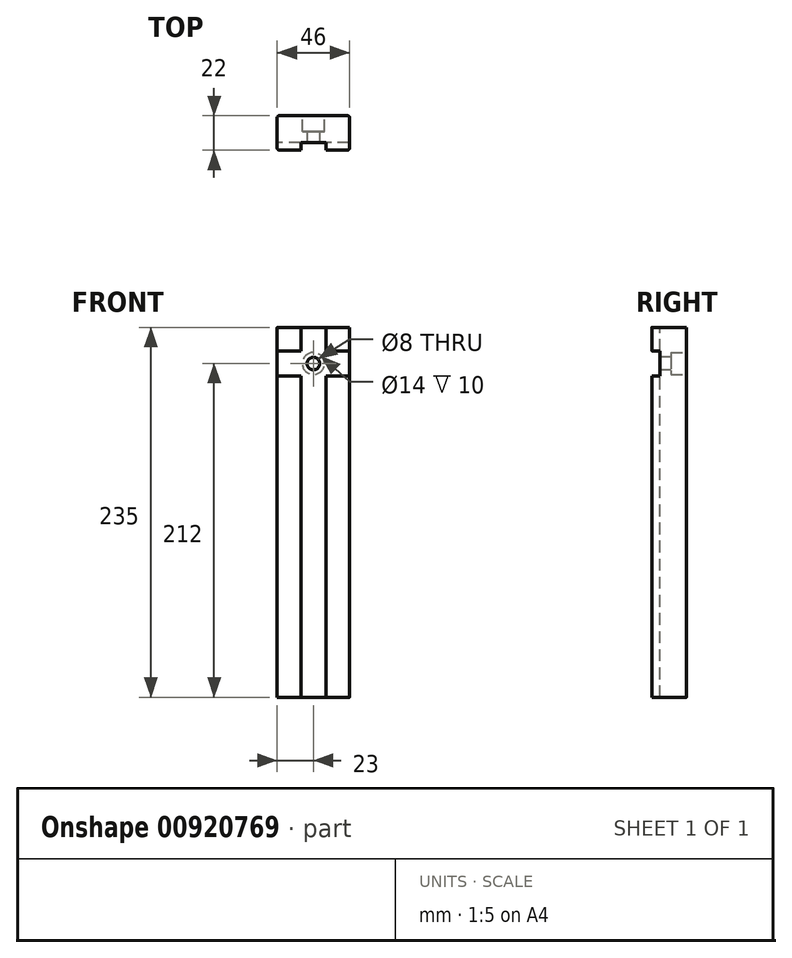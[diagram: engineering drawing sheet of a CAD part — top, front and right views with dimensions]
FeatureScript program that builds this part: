
annotation { "Feature Type Name" : "Feature", "Feature Type Description" : "" }
export const myFeature = defineFeature(function(context is Context, id is Id, definition is map)
    precondition{}
    {
        {
            var Q0;
            Q0=qCreatedBy(makeId("Top.planeOp"),FACE);
            var sketch = newSketch(context, id + "F0", { "sketchPlane" : qUnion([Q0])});
            skLineSegment(sketch, "E0.bottom", {"start": v(0, 0) * mm, "end": v(46, 0) * mm});
            skLineSegment(sketch, "E0.top", {"start": v(0, 22) * mm, "end": v(46, 22) * mm});
            skLineSegment(sketch, "E0.left", {"start": v(0, 0) * mm, "end": v(0, 22) * mm});
            skLineSegment(sketch, "E0.right", {"start": v(46, 0) * mm, "end": v(46, 22) * mm});
            skSolve(sketch);
        }
        {
            var Q0;
            Q0 = qSketchRegion(id + "F0", true);
            extrude(context, id + "F1", {"entities" : qUnion([Q0]), "depth" : 235 * mm, "offsetDistance" : 25 * mm});
        }
        {
            var Q0;
            Q0=makeQuery(id+"F1.opExtrude","SWEPT_EDGE",EDGE,{"disambiguationData":[OSD([sQuery(id+"F0.wireOp",EDGE,"E0.bottom"),sQuery(id+"F0.wireOp",EDGE,"E0.right")])]});
            var Q1;
            Q1=makeQuery(id+"F1.opExtrude","SWEPT_EDGE",EDGE,{"disambiguationData":[OSD([sQuery(id+"F0.wireOp",EDGE,"E0.top"),sQuery(id+"F0.wireOp",EDGE,"E0.right")])]});
            var Q2;
            Q2=makeQuery(id+"F1.opExtrude","SWEPT_EDGE",EDGE,{"disambiguationData":[OSD([sQuery(id+"F0.wireOp",EDGE,"E0.bottom"),sQuery(id+"F0.wireOp",EDGE,"E0.left")])]});
            var Q3;
            Q3=makeQuery(id+"F1.opExtrude","SWEPT_EDGE",EDGE,{"disambiguationData":[OSD([sQuery(id+"F0.wireOp",EDGE,"E0.top"),sQuery(id+"F0.wireOp",EDGE,"E0.left")])]});
            fillet(context, id + "F2", {"entities" : qUnion([Q0, Q1, Q2, Q3]), "radius" : 1.5 * mm, "tangentPropagation" : true, "allowEdgeOverflow" : false});
        }
        {
            var Q0;
            Q0=makeQuery(id+"F1.opExtrude","SWEPT_FACE",FACE,{"disambiguationData":[OSD([sQuery(id+"F0.wireOp",EDGE,"E0.left")])]});
            var sketch = newSketch(context, id + "F3", { "sketchPlane" : qUnion([Q0])});
            skLineSegment(sketch, "E1.bottom", {"start": v(-5, 220) * mm, "end": v(0, 220) * mm});
            skLineSegment(sketch, "E1.top", {"start": v(-5, 204) * mm, "end": v(0, 204) * mm});
            skLineSegment(sketch, "E1.left", {"start": v(-5, 220) * mm, "end": v(-5, 204) * mm});
            skLineSegment(sketch, "E1.right", {"start": v(0, 220) * mm, "end": v(0, 204) * mm});
            skSolve(sketch);
        }
        {
            var Q0;
            {var subQ0=sQuery(id+"F3.wireOp",EDGE,"E1.left");Q0=makeQuery(id+"F3.imprint","IMPRINT",FACE,{"disambiguationData":[TD([[makeQuery(id+"F3.imprint","IMPRINT",EDGE,{"derivedFrom":subQ0}),1.0]])]});}
            var Q1;
            {var subQ0=sQuery(id+"F3.wireOp",EDGE,"E1.right");Q1=makeQuery(id+"F3.imprint","IMPRINT",FACE,{"disambiguationData":[TD([[makeQuery(id+"F3.imprint","IMPRINT",EDGE,{"derivedFrom":subQ0}),-1.0]])]});}
            extrude(context, id + "F4", {"entities" : qUnion([Q0, Q1]), "operationType" : NewBodyOperationType.REMOVE, "endBound" : BoundingType.THROUGH_ALL, "oppositeDirection" : true, "depth" : 25 * mm, "offsetDistance" : 25 * mm});
        }
        {
            var Q0;
            Q0=makeQuery(id+"F1.opExtrude","CAP_FACE",FACE,{"disambiguationData":[OSD([sQuery(id+"F0.wireOp",EDGE,"E0.bottom"),sQuery(id+"F0.wireOp",EDGE,"E0.top"),sQuery(id+"F0.wireOp",EDGE,"E0.left"),sQuery(id+"F0.wireOp",EDGE,"E0.right")])],"isStart":false});
            var sketch = newSketch(context, id + "F5", { "sketchPlane" : qUnion([Q0])});
            skLineSegment(sketch, "E2.bottom", {"start": v(31, 0) * mm, "end": v(15, 0) * mm});
            skLineSegment(sketch, "E2.top", {"start": v(31, 5) * mm, "end": v(15, 5) * mm});
            skLineSegment(sketch, "E2.left", {"start": v(31, 0) * mm, "end": v(31, 5) * mm});
            skLineSegment(sketch, "E2.right", {"start": v(15, 0) * mm, "end": v(15, 5) * mm});
            skLineSegment(sketch, "E3", {"start": v(15, 2.5) * mm, "end": v(0, 2.5) * mm, "construction": true});
            skLineSegment(sketch, "E4", {"start": v(31, 2.5) * mm, "end": v(46, 2.5) * mm, "construction": true});
            skSolve(sketch);
        }
        {
            var Q0;
            Q0=makeQuery(id+"F5.imprint","IMPRINT",FACE,{"disambiguationData":[TD([[makeQuery(id+"F5.imprint","IMPRINT",EDGE,{"derivedFrom":sQuery(id+"F5.wireOp",EDGE,"E2.bottom")}),1.0]])]});
            extrude(context, id + "F6", {"entities" : qUnion([Q0]), "operationType" : NewBodyOperationType.REMOVE, "endBound" : BoundingType.THROUGH_ALL, "oppositeDirection" : true, "depth" : 25 * mm, "offsetDistance" : 25 * mm});
        }
        {
            var Q0;
            Q0=makeQuery(id+"F6.boolean.opBoolean","MERGE",FACE,{"derivedFrom":[makeQuery(id+"F4.boolean.opBoolean","COPY",FACE,{"derivedFrom":makeQuery(id+"F4.opExtrude","SWEPT_FACE",FACE,{"disambiguationData":[OSD([sQuery(id+"F3.wireOp",EDGE,"E1.left")])]})})],"fromTools":[makeQuery(id+"F6.opExtrude","SWEPT_FACE",FACE,{"disambiguationData":[OSD([sQuery(id+"F5.wireOp",EDGE,"E2.top")])]})]});
            var sketch = newSketch(context, id + "F7", { "sketchPlane" : qUnion([Q0])});
            skLineSegment(sketch, "E5", {"start": v(15, 220) * mm, "end": v(31, 204) * mm, "construction": true});
            skLineSegment(sketch, "E6", {"start": v(31, 220) * mm, "end": v(15, 204) * mm, "construction": true});
            skPoint(sketch, "E7", {"position": v(23, 212) * mm});
            skCircle(sketch, "E8", {"center": v(23, 212) * mm, "radius": 4 * mm});
            skSolve(sketch);
        }
        {
            var Q0;
            Q0=makeQuery(id+"F7.imprint","IMPRINT",FACE,{"disambiguationData":[TD([[makeQuery(id+"F7.imprint","IMPRINT",EDGE,{"derivedFrom":sQuery(id+"F7.wireOp",EDGE,"E8")}),1.0]])]});
            extrude(context, id + "F8", {"entities" : qUnion([Q0]), "operationType" : NewBodyOperationType.REMOVE, "endBound" : BoundingType.THROUGH_ALL, "oppositeDirection" : true, "depth" : 25 * mm, "offsetDistance" : 25 * mm});
        }
        {
            var Q0;
            Q0=makeQuery(id+"F1.opExtrude","SWEPT_FACE",FACE,{"disambiguationData":[OSD([sQuery(id+"F0.wireOp",EDGE,"E0.top")])]});
            var sketch = newSketch(context, id + "F9", { "sketchPlane" : qUnion([Q0])});
            skCircle(sketch, "E9", {"center": v(-23, 212) * mm, "radius": 7 * mm});
            skSolve(sketch);
        }
        {
            var Q0;
            Q0=makeQuery(id+"F9.imprint","IMPRINT",FACE,{"disambiguationData":[TD([[makeQuery(id+"F9.imprint","IMPRINT",EDGE,{"derivedFrom":sQuery(id+"F9.wireOp",EDGE,"E9")}),1.0]])]});
            extrude(context, id + "F10", {"entities" : qUnion([Q0]), "operationType" : NewBodyOperationType.REMOVE, "oppositeDirection" : true, "depth" : 10 * mm, "offsetDistance" : 25 * mm});
        }
    });
